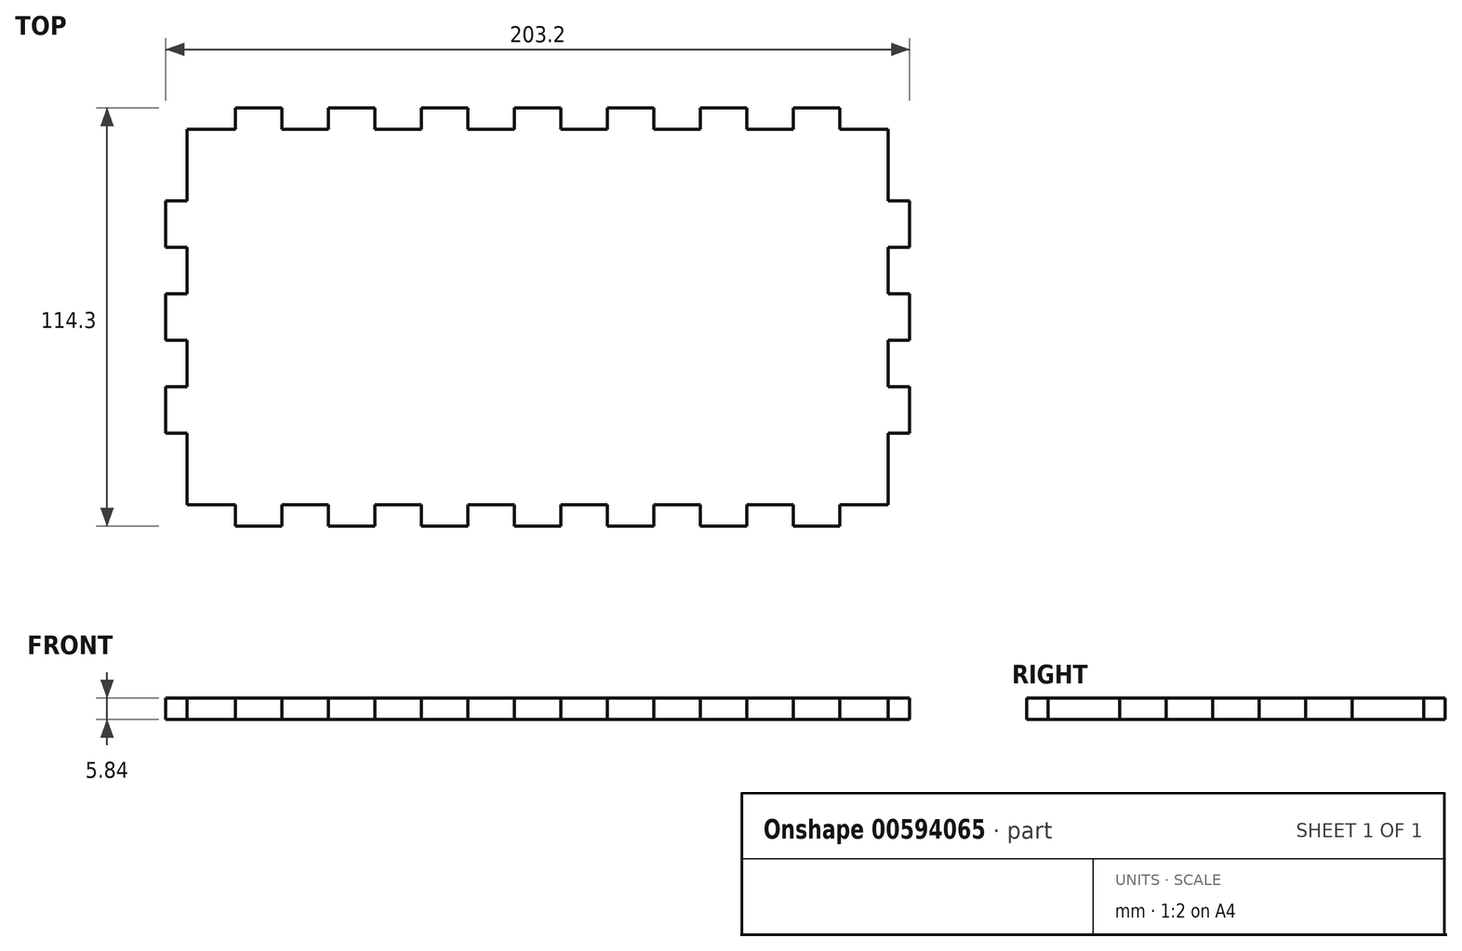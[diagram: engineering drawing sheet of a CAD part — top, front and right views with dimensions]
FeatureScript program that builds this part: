
annotation { "Feature Type Name" : "Feature", "Feature Type Description" : "" }
export const myFeature = defineFeature(function(context is Context, id is Id, definition is map)
    precondition{}
    {
        {
            var Q0;
            Q0=qCreatedBy(makeId("Top.planeOp"),FACE);
            var sketch = newSketch(context, id + "F0", { "sketchPlane" : qUnion([Q0])});
            skLineSegment(sketch, "E0.bottom", {"start": v(19.05, 0) * mm, "end": v(31.75, 0) * mm});
            skLineSegment(sketch, "E0.left", {"start": v(0, -25.4) * mm, "end": v(0, -38.1) * mm});
            skPoint(sketch, "E1.orphan", {"position": v(0, 0) * mm});
            skLineSegment(sketch, "E2", {"start": v(19.05, -5.84) * mm, "end": v(19.05, 0) * mm});
            skLineSegment(sketch, "E3", {"start": v(19.05, -5.84) * mm, "end": v(5.84, -5.84) * mm});
            skLineSegment(sketch, "E4", {"start": v(31.75, 0) * mm, "end": v(31.75, -5.84) * mm});
            skLineSegment(sketch, "E5", {"start": v(31.75, -5.84) * mm, "end": v(44.45, -5.84) * mm});
            skLineSegment(sketch, "E6", {"start": v(44.45, -5.84) * mm, "end": v(44.45, 0) * mm});
            skLineSegment(sketch, "E7", {"start": v(44.45, 0) * mm, "end": v(57.15, 0) * mm});
            skLineSegment(sketch, "E8", {"start": v(57.15, 0) * mm, "end": v(57.15, -5.84) * mm});
            skLineSegment(sketch, "E9", {"start": v(57.15, -5.84) * mm, "end": v(69.85, -5.84) * mm});
            skLineSegment(sketch, "E10", {"start": v(69.85, -5.84) * mm, "end": v(69.85, 0) * mm});
            skLineSegment(sketch, "E11", {"start": v(69.85, 0) * mm, "end": v(82.55, 0) * mm});
            skLineSegment(sketch, "E12", {"start": v(82.55, 0) * mm, "end": v(82.55, -5.84) * mm});
            skLineSegment(sketch, "E13", {"start": v(82.55, -5.84) * mm, "end": v(95.25, -5.84) * mm});
            skLineSegment(sketch, "E14", {"start": v(95.25, -5.84) * mm, "end": v(95.25, 0) * mm});
            skLineSegment(sketch, "E15.trimOffspring", {"start": v(95.25, 0) * mm, "end": v(107.95, 0) * mm});
            skLineSegment(sketch, "E16", {"start": v(107.95, 0) * mm, "end": v(107.95, -5.84) * mm});
            skLineSegment(sketch, "E17", {"start": v(107.95, -5.84) * mm, "end": v(120.65, -5.84) * mm});
            skLineSegment(sketch, "E18", {"start": v(120.65, -5.84) * mm, "end": v(120.65, 0) * mm});
            skLineSegment(sketch, "E19", {"start": v(120.65, 0) * mm, "end": v(133.35, 0) * mm});
            skLineSegment(sketch, "E20", {"start": v(133.35, 0) * mm, "end": v(133.35, -5.84) * mm});
            skLineSegment(sketch, "E21", {"start": v(133.35, -5.84) * mm, "end": v(146.05, -5.84) * mm});
            skLineSegment(sketch, "E22", {"start": v(146.05, -5.84) * mm, "end": v(146.05, 0) * mm});
            skLineSegment(sketch, "E23.trimOffspring", {"start": v(146.05, 0) * mm, "end": v(158.75, 0) * mm});
            skLineSegment(sketch, "E24", {"start": v(158.75, 0) * mm, "end": v(158.75, -5.84) * mm});
            skLineSegment(sketch, "E25", {"start": v(158.75, -5.84) * mm, "end": v(171.45, -5.84) * mm});
            skLineSegment(sketch, "E26", {"start": v(171.45, -5.84) * mm, "end": v(171.45, 0) * mm});
            skLineSegment(sketch, "E27", {"start": v(171.45, 0) * mm, "end": v(184.15, 0) * mm});
            skLineSegment(sketch, "E28", {"start": v(184.15, 0) * mm, "end": v(184.15, -5.84) * mm});
            skPoint(sketch, "E29.orphan", {"position": v(203.2, 0) * mm});
            skLineSegment(sketch, "E30", {"start": v(5.84, -5.84) * mm, "end": v(5.84, -25.4) * mm});
            skLineSegment(sketch, "E31", {"start": v(5.84, -25.4) * mm, "end": v(0, -25.4) * mm});
            skLineSegment(sketch, "E32", {"start": v(0, -38.1) * mm, "end": v(5.84, -38.1) * mm});
            skLineSegment(sketch, "E33", {"start": v(5.84, -38.1) * mm, "end": v(5.84, -50.8) * mm});
            skLineSegment(sketch, "E34", {"start": v(5.84, -50.8) * mm, "end": v(0, -50.8) * mm});
            skLineSegment(sketch, "E35", {"start": v(0, -50.8) * mm, "end": v(0, -63.5) * mm});
            skLineSegment(sketch, "E36", {"start": v(0, -63.5) * mm, "end": v(5.84, -63.5) * mm});
            skLineSegment(sketch, "E37", {"start": v(5.84, -63.5) * mm, "end": v(5.84, -76.2) * mm});
            skLineSegment(sketch, "E38", {"start": v(5.84, -76.2) * mm, "end": v(0, -76.2) * mm});
            skLineSegment(sketch, "E39.trimOffspring", {"start": v(0, -76.2) * mm, "end": v(0, -88.9) * mm});
            skLineSegment(sketch, "E40", {"start": v(0, -88.9) * mm, "end": v(5.84, -88.9) * mm});
            skLineSegment(sketch, "E41", {"start": v(5.84, -88.9) * mm, "end": v(5.84, -108.46) * mm});
            skLineSegment(sketch, "E42", {"start": v(5.84, -108.46) * mm, "end": v(19.05, -108.46) * mm});
            skLineSegment(sketch, "E43", {"start": v(19.05, -108.46) * mm, "end": v(19.05, -114.3) * mm});
            skPoint(sketch, "E44.orphan", {"position": v(0, -114.3) * mm});
            skLineSegment(sketch, "E45", {"start": v(101.6, 0) * mm, "end": v(101.6, -19.05) * mm, "construction": true});
            skLineSegment(sketch, "E46", {"start": v(0, -57.15) * mm, "end": v(19.05, -57.15) * mm, "construction": true});
            skLineSegment(sketch, "E47.MirrorCS", {"start": v(197.36, -5.84) * mm, "end": v(197.36, -25.4) * mm});
            skLineSegment(sketch, "E48.MirrorCS", {"start": v(197.36, -25.4) * mm, "end": v(203.2, -25.4) * mm});
            skLineSegment(sketch, "E49.MirrorCS", {"start": v(203.2, -25.4) * mm, "end": v(203.2, -38.1) * mm});
            skLineSegment(sketch, "E50.MirrorCS", {"start": v(203.2, -38.1) * mm, "end": v(197.36, -38.1) * mm});
            skLineSegment(sketch, "E51.MirrorCS", {"start": v(197.36, -38.1) * mm, "end": v(197.36, -50.8) * mm});
            skLineSegment(sketch, "E52.MirrorCS", {"start": v(197.36, -50.8) * mm, "end": v(203.2, -50.8) * mm});
            skLineSegment(sketch, "E53.MirrorCS", {"start": v(203.2, -50.8) * mm, "end": v(203.2, -63.5) * mm});
            skLineSegment(sketch, "E54.MirrorCS", {"start": v(203.2, -63.5) * mm, "end": v(197.36, -63.5) * mm});
            skLineSegment(sketch, "E55.MirrorCS", {"start": v(197.36, -63.5) * mm, "end": v(197.36, -76.2) * mm});
            skLineSegment(sketch, "E56.MirrorCS", {"start": v(197.36, -76.2) * mm, "end": v(203.2, -76.2) * mm});
            skLineSegment(sketch, "E57.MirrorCS", {"start": v(203.2, -76.2) * mm, "end": v(203.2, -88.9) * mm});
            skLineSegment(sketch, "E58.MirrorCS", {"start": v(203.2, -88.9) * mm, "end": v(197.36, -88.9) * mm});
            skLineSegment(sketch, "E59.MirrorCS", {"start": v(197.36, -88.9) * mm, "end": v(197.36, -108.46) * mm});
            skLineSegment(sketch, "E60.MirrorCS", {"start": v(197.36, -108.46) * mm, "end": v(184.15, -108.46) * mm});
            skLineSegment(sketch, "E61.MirrorCS", {"start": v(184.15, -108.46) * mm, "end": v(184.15, -114.3) * mm});
            skLineSegment(sketch, "E62", {"start": v(184.15, -5.84) * mm, "end": v(197.36, -5.84) * mm});
            skLineSegment(sketch, "E63.MirrorCS", {"start": v(19.05, -114.3) * mm, "end": v(31.75, -114.3) * mm});
            skLineSegment(sketch, "E64.MirrorCS", {"start": v(31.75, -114.3) * mm, "end": v(31.75, -108.46) * mm});
            skLineSegment(sketch, "E65.MirrorCS", {"start": v(31.75, -108.46) * mm, "end": v(44.45, -108.46) * mm});
            skLineSegment(sketch, "E66.MirrorCS", {"start": v(44.45, -108.46) * mm, "end": v(44.45, -114.3) * mm});
            skLineSegment(sketch, "E67.MirrorCS", {"start": v(44.45, -114.3) * mm, "end": v(57.15, -114.3) * mm});
            skLineSegment(sketch, "E68.MirrorCS", {"start": v(57.15, -114.3) * mm, "end": v(57.15, -108.46) * mm});
            skLineSegment(sketch, "E69.MirrorCS", {"start": v(57.15, -108.46) * mm, "end": v(69.85, -108.46) * mm});
            skLineSegment(sketch, "E70.MirrorCS", {"start": v(69.85, -108.46) * mm, "end": v(69.85, -114.3) * mm});
            skLineSegment(sketch, "E71.MirrorCS", {"start": v(69.85, -114.3) * mm, "end": v(82.55, -114.3) * mm});
            skLineSegment(sketch, "E72.MirrorCS", {"start": v(82.55, -114.3) * mm, "end": v(82.55, -108.46) * mm});
            skLineSegment(sketch, "E73.MirrorCS", {"start": v(82.55, -108.46) * mm, "end": v(95.25, -108.46) * mm});
            skLineSegment(sketch, "E74.MirrorCS", {"start": v(95.25, -108.46) * mm, "end": v(95.25, -114.3) * mm});
            skLineSegment(sketch, "E75.MirrorCS", {"start": v(95.25, -114.3) * mm, "end": v(107.95, -114.3) * mm});
            skLineSegment(sketch, "E76.MirrorCS", {"start": v(107.95, -114.3) * mm, "end": v(107.95, -108.46) * mm});
            skLineSegment(sketch, "E77.MirrorCS", {"start": v(107.95, -108.46) * mm, "end": v(120.65, -108.46) * mm});
            skLineSegment(sketch, "E78.MirrorCS", {"start": v(120.65, -108.46) * mm, "end": v(120.65, -114.3) * mm});
            skLineSegment(sketch, "E79.MirrorCS", {"start": v(120.65, -114.3) * mm, "end": v(133.35, -114.3) * mm});
            skLineSegment(sketch, "E80.MirrorCS", {"start": v(133.35, -114.3) * mm, "end": v(133.35, -108.46) * mm});
            skLineSegment(sketch, "E81.MirrorCS", {"start": v(133.35, -108.46) * mm, "end": v(146.05, -108.46) * mm});
            skLineSegment(sketch, "E82.MirrorCS", {"start": v(146.05, -108.46) * mm, "end": v(146.05, -114.3) * mm});
            skLineSegment(sketch, "E83.MirrorCS", {"start": v(146.05, -114.3) * mm, "end": v(158.75, -114.3) * mm});
            skLineSegment(sketch, "E84.MirrorCS", {"start": v(158.75, -114.3) * mm, "end": v(158.75, -108.46) * mm});
            skLineSegment(sketch, "E85.MirrorCS", {"start": v(158.75, -108.46) * mm, "end": v(171.45, -108.46) * mm});
            skLineSegment(sketch, "E86.MirrorCS", {"start": v(171.45, -108.46) * mm, "end": v(171.45, -114.3) * mm});
            skLineSegment(sketch, "E87.MirrorCS", {"start": v(171.45, -114.3) * mm, "end": v(184.15, -114.3) * mm});
            skSolve(sketch);
        }
        {
            var Q0;
            Q0=makeQuery(id+"F0.imprint","IMPRINT",FACE,{"disambiguationData":[TD([[makeQuery(id+"F0.imprint","IMPRINT",EDGE,{"derivedFrom":sQuery(id+"F0.wireOp",EDGE,"E2")}),-1.0]])]});
            extrude(context, id + "F1", {"entities" : qUnion([Q0]), "depth" : 5.84 * mm, "offsetDistance" : 25.4 * mm});
        }
    });
